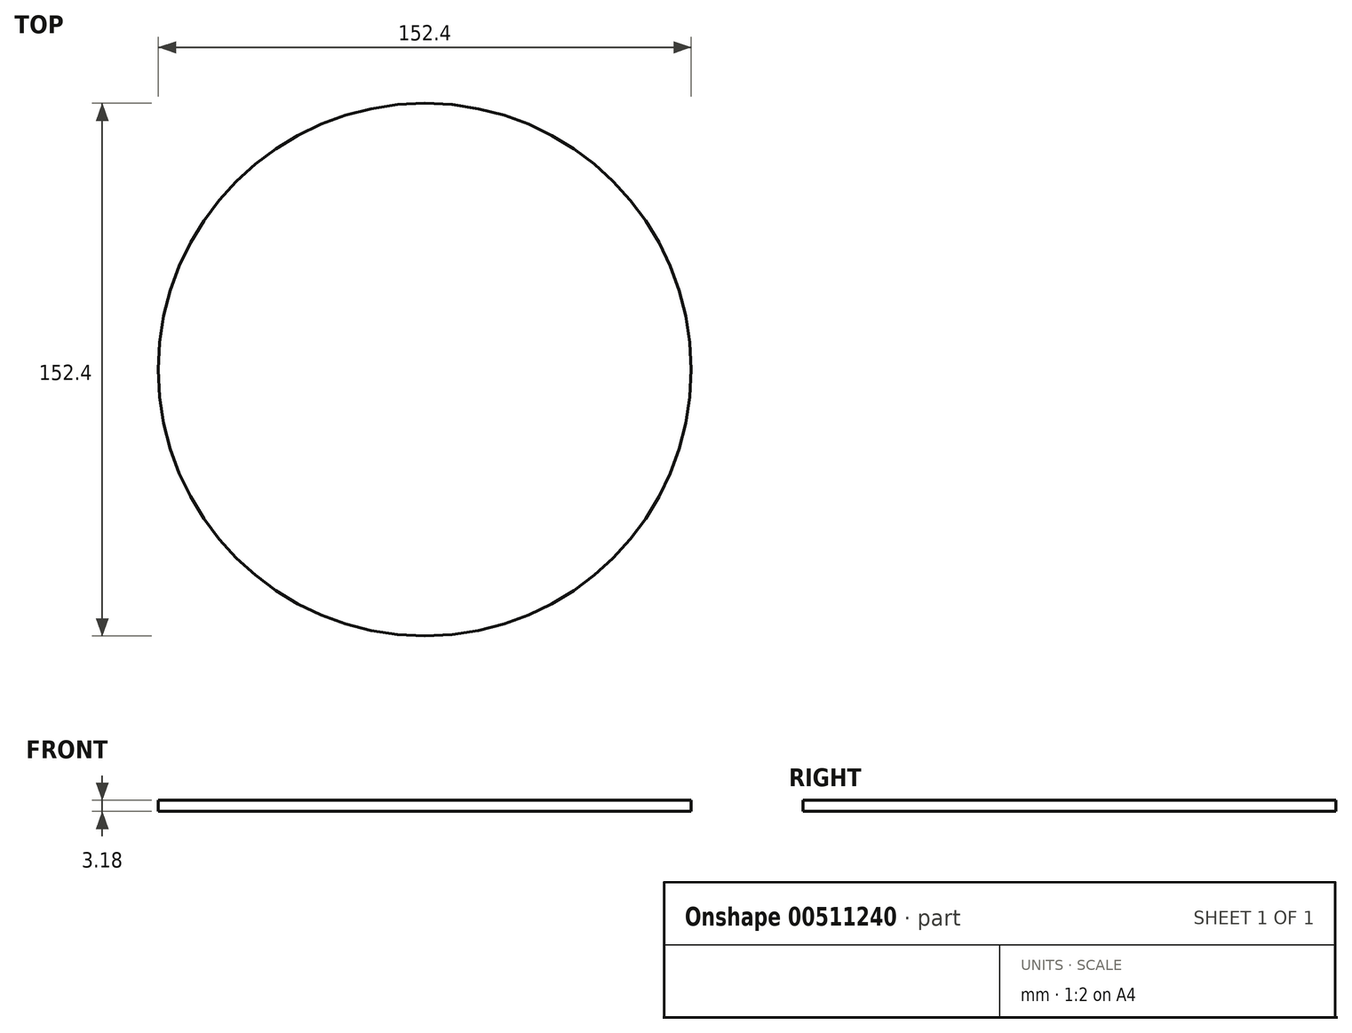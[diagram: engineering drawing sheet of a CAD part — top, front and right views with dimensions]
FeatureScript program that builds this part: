
annotation { "Feature Type Name" : "Feature", "Feature Type Description" : "" }
export const myFeature = defineFeature(function(context is Context, id is Id, definition is map)
    precondition{}
    {
        {
            var Q0;
            Q0=qCreatedBy(makeId("Top.planeOp"),FACE);
            var sketch = newSketch(context, id + "F0", { "sketchPlane" : qUnion([Q0])});
            skCircle(sketch, "E0", {"center": v(0, 0) * mm, "radius": 76.2 * mm});
            skSolve(sketch);
        }
        {
            var Q0;
            Q0=makeQuery(id+"F0.imprint","IMPRINT",FACE,{"disambiguationData":[TD([[makeQuery(id+"F0.imprint","IMPRINT",EDGE,{"derivedFrom":sQuery(id+"F0.wireOp",EDGE,"E0")}),1.0]])]});
            extrude(context, id + "F1", {"entities" : qUnion([Q0]), "depth" : 3.17 * mm});
        }
    });
